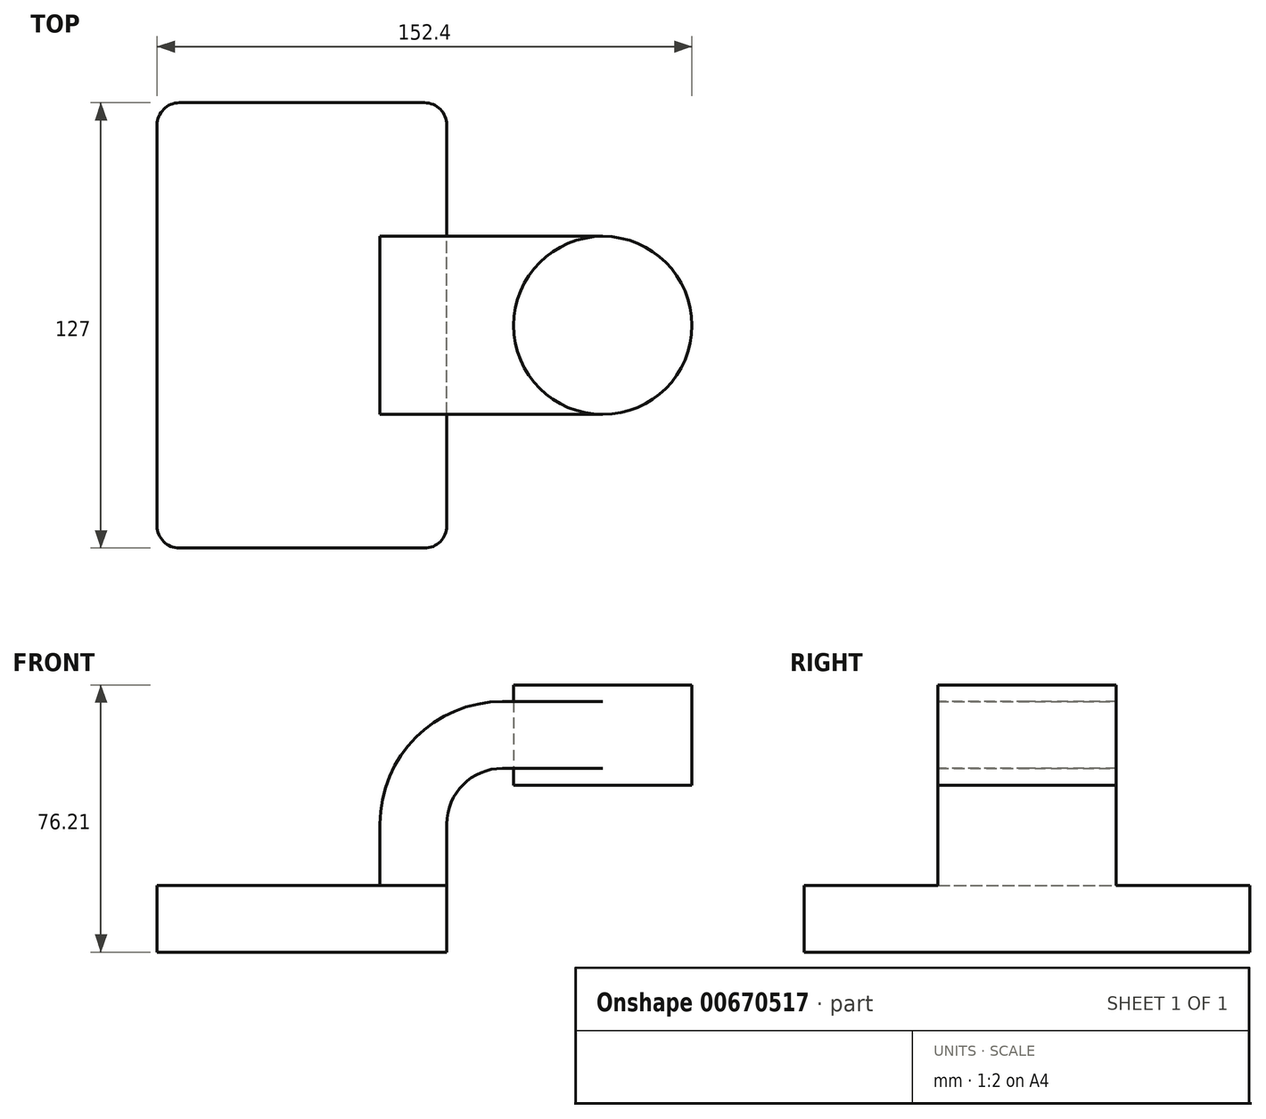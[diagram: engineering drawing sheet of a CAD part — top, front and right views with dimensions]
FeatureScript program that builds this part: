
annotation { "Feature Type Name" : "Feature", "Feature Type Description" : "" }
export const myFeature = defineFeature(function(context is Context, id is Id, definition is map)
    precondition{}
    {
        {
            var Q0;
            Q0=qCreatedBy(makeId("Front.planeOp"),FACE);
            var sketch = newSketch(context, id + "F0", { "sketchPlane" : qUnion([Q0])});
            skLineSegment(sketch, "E0.bottom", {"start": v(-41.27, -9.53) * mm, "end": v(41.28, -9.53) * mm});
            skLineSegment(sketch, "E0.top", {"start": v(-41.28, 9.52) * mm, "end": v(41.28, 9.52) * mm});
            skLineSegment(sketch, "E0.left", {"start": v(-41.28, -9.53) * mm, "end": v(-41.28, 9.52) * mm});
            skLineSegment(sketch, "E0.right", {"start": v(41.28, -9.53) * mm, "end": v(41.28, 9.52) * mm});
            skPoint(sketch, "E0.middle", {"position": v(0, 0) * mm});
            skLineSegment(sketch, "E1.bottom", {"start": v(60.32, 38.1) * mm, "end": v(111.12, 38.1) * mm});
            skLineSegment(sketch, "E1.top", {"start": v(60.32, 66.68) * mm, "end": v(111.12, 66.68) * mm});
            skLineSegment(sketch, "E1.left", {"start": v(60.32, 38.1) * mm, "end": v(60.32, 66.67) * mm});
            skLineSegment(sketch, "E1.right", {"start": v(111.12, 38.1) * mm, "end": v(111.12, 66.67) * mm});
            skPoint(sketch, "E1.middle", {"position": v(85.72, 52.39) * mm});
            skLineSegment(sketch, "E2", {"start": v(41.27, 9.52) * mm, "end": v(41.27, 27) * mm});
            skArc(sketch, "E3", {"start": v(41.28, 27) * mm, "mid": v(45.92, 38.23) * mm, "end": v(57.15, 42.88) * mm});
            skLineSegment(sketch, "E4", {"start": v(57.15, 42.88) * mm, "end": v(85.72, 42.88) * mm});
            skLineSegment(sketch, "E5.0", {"start": v(57.15, 61.93) * mm, "end": v(85.72, 61.93) * mm});
            skArc(sketch, "E5.1", {"start": v(22.23, 27) * mm, "mid": v(32.45, 51.7) * mm, "end": v(57.15, 61.93) * mm});
            skLineSegment(sketch, "E5.2", {"start": v(22.23, 9.52) * mm, "end": v(22.23, 27) * mm});
            skLineSegment(sketch, "E6", {"start": v(85.72, 38.1) * mm, "end": v(85.72, 66.68) * mm});
            skFitSpline(sketch, "E7", {"points": [v(-41.28, 9.53) * mm, v(57.15, 61.93) * mm], "startDerivative": vector(1.78, 85.42) * mm, "endDerivative": vector(130, -0.01) * mm});
            skSolve(sketch);
        }
        {
            var Q0;
            Q0=makeQuery(id+"F0.imprint","IMPRINT",FACE,{"disambiguationData":[TD([[makeQuery(id+"F0.imprint","IMPRINT",EDGE,{"derivedFrom":sQuery(id+"F0.wireOp",EDGE,"E0.bottom")}),1.0]])]});
            extrude(context, id + "F1", {"entities" : qUnion([Q0]), "endBound" : BoundingType.SYMMETRIC, "depth" : 127 * mm, "offsetDistance" : 25.4 * mm});
        }
        {
            var Q0;
            {var subQ1=sQuery(id+"F0.wireOp",EDGE,"E2");Q0=makeQuery(id+"F0.imprint","IMPRINT",FACE,{"disambiguationData":[TD([[makeQuery(id+"F0.imprint","IMPRINT",EDGE,{"derivedFrom":subQ1}),1.0]])]});}
            var Q1;
            {var subQ0=sQuery(id+"F0.wireOp",EDGE,"E4");var subQ1=sQuery(id+"F0.wireOp",EDGE,"E1.left");var subQ2=makeQuery(id+"F0.imprint","INTERSECT",VERTEX,{"derivedFrom":[subQ1,subQ0]});Q1=makeQuery(id+"F0.imprint","IMPRINT",FACE,{"disambiguationData":[TD([[makeQuery(id+"F0.imprint","IMPRINT",EDGE,{"disambiguationData":[TD([[subQ2,-1.0]])],"derivedFrom":subQ1}),-1.0]])]});}
            extrude(context, id + "F2", {"entities" : qUnion([Q0, Q1]), "operationType" : NewBodyOperationType.ADD, "endBound" : BoundingType.SYMMETRIC, "depth" : 50.8 * mm, "offsetDistance" : 25.4 * mm});
        }
        {
            var Q0;
            Q0=makeQuery(id+"F0.imprint","IMPRINT",FACE,{"disambiguationData":[TD([[makeQuery(id+"F0.imprint","IMPRINT",EDGE,{"derivedFrom":sQuery(id+"F0.wireOp",EDGE,"E5.1")}),1.0]])]});
            extrude(context, id + "F3", {"entities" : qUnion([Q0]), "operationType" : NewBodyOperationType.ADD, "endBound" : BoundingType.SYMMETRIC, "depth" : 15.88 * mm, "offsetDistance" : 25.4 * mm});
        }
        {
            var Q0;
            {var subQ0=sQuery(id+"F0.wireOp",EDGE,"E1.right");Q0=makeQuery(id+"F0.imprint","IMPRINT",FACE,{"disambiguationData":[TD([[makeQuery(id+"F0.imprint","IMPRINT",EDGE,{"derivedFrom":subQ0}),1.0]])]});}
            var Q1;
            Q1=sQuery(id+"F0.wireOp",EDGE,"E1.right");
            var Q2;
            Q2=sQuery(id+"F0.wireOp",EDGE,"E6");
            revolve(context, id + "F4", {"entities" : qUnion([Q0]), "surfaceEntities" : qUnion([Q1]), "axis" : qUnion([Q2]), "revolveType" : RevolveType.FULL});
        }
        {
            var Q0;
            Q0=makeQuery(id+"F1.opExtrude","CAP_EDGE",EDGE,{"disambiguationData":[OSD([sQuery(id+"F0.wireOp",EDGE,"E0.left")])],"isStart":false});
            var Q1;
            Q1=makeQuery(id+"F1.opExtrude","CAP_EDGE",EDGE,{"disambiguationData":[OSD([sQuery(id+"F0.wireOp",EDGE,"E0.right")])],"isStart":false});
            var Q2;
            Q2=makeQuery(id+"F1.opExtrude","CAP_EDGE",EDGE,{"disambiguationData":[OSD([sQuery(id+"F0.wireOp",EDGE,"E0.left")])],"isStart":true});
            var Q3;
            Q3=makeQuery(id+"F1.opExtrude","CAP_EDGE",EDGE,{"disambiguationData":[OSD([sQuery(id+"F0.wireOp",EDGE,"E0.right")])],"isStart":true});
            fillet(context, id + "F5", {"entities" : qUnion([Q0, Q1, Q2, Q3]), "radius" : 6.35 * mm, "tangentPropagation" : true, "allowEdgeOverflow" : false});
        }
    });
